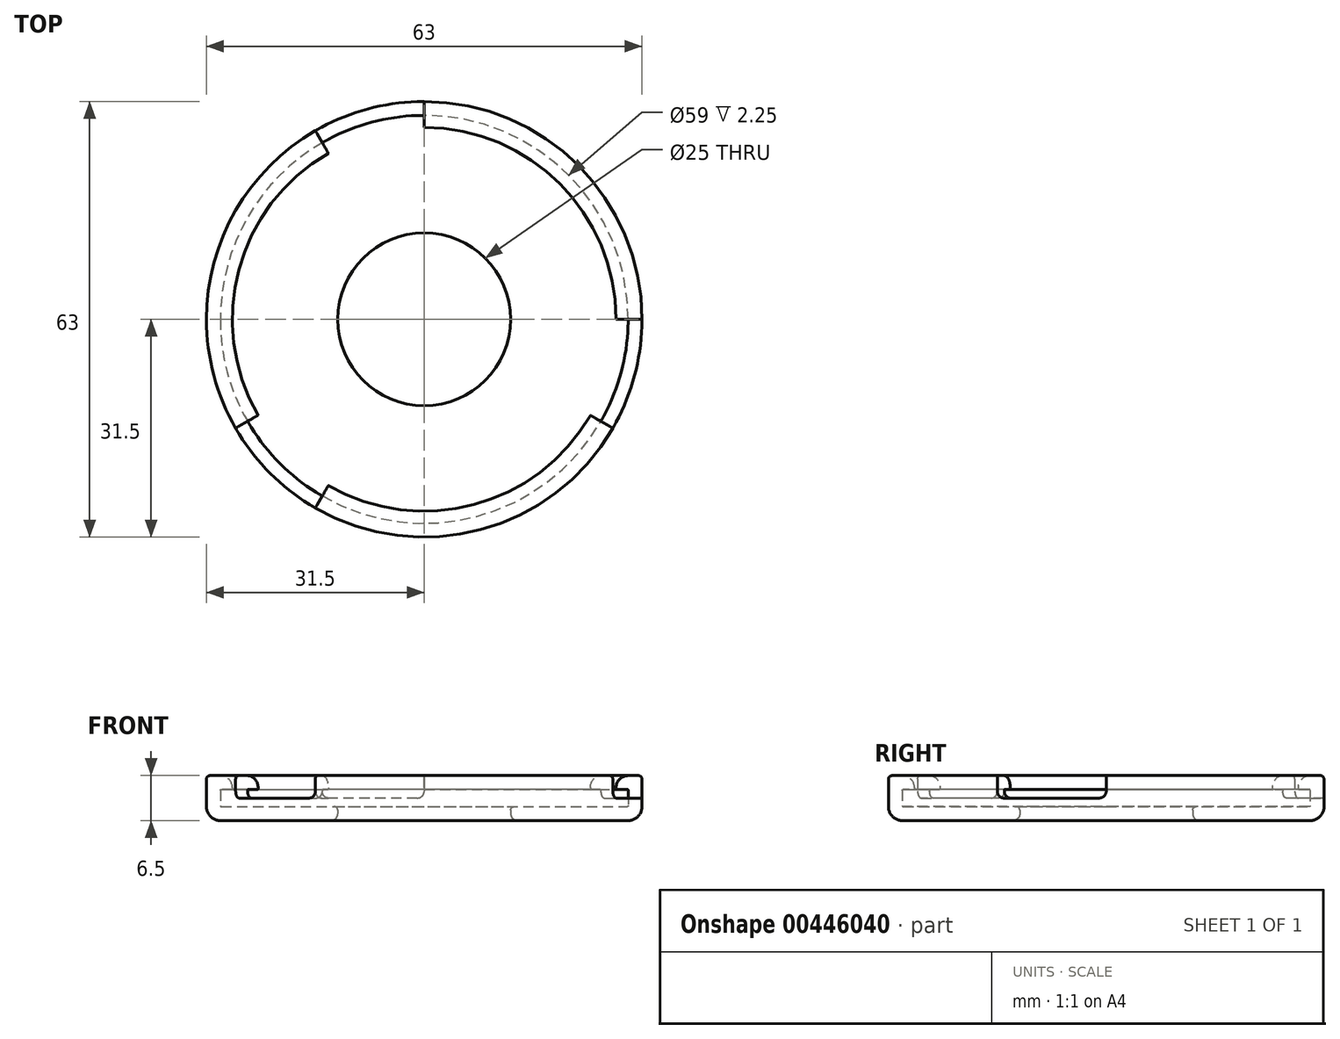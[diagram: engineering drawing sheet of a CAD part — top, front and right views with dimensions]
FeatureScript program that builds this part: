
annotation { "Feature Type Name" : "Feature", "Feature Type Description" : "" }
export const myFeature = defineFeature(function(context is Context, id is Id, definition is map)
    precondition{}
    {
        {
            var Q0;
            Q0=qCreatedBy(makeId("Front.planeOp"),FACE);
            var sketch = newSketch(context, id + "F0", { "sketchPlane" : qUnion([Q0])});
            skLineSegment(sketch, "E0", {"start": v(13.5, 0) * mm, "end": v(29.5, 0) * mm});
            skLineSegment(sketch, "E1", {"start": v(31.5, 2) * mm, "end": v(31.5, 6) * mm});
            skLineSegment(sketch, "E2", {"start": v(31, 6.5) * mm, "end": v(29.5, 6.5) * mm});
            skLineSegment(sketch, "E3", {"start": v(27.75, 4.75) * mm, "end": v(27.75, 4.63) * mm});
            skLineSegment(sketch, "E4", {"start": v(27.88, 4.5) * mm, "end": v(29.38, 4.5) * mm});
            skLineSegment(sketch, "E5", {"start": v(29.5, 4.38) * mm, "end": v(29.5, 2.13) * mm});
            skLineSegment(sketch, "E6", {"start": v(29.38, 2) * mm, "end": v(13, 2) * mm});
            skLineSegment(sketch, "E7", {"start": v(12.5, 1.5) * mm, "end": v(12.5, 1) * mm});
            skPoint(sketch, "E8.visualSharp", {"position": v(31.5, 0) * mm});
            skArc(sketch, "E8.filletArc", {"start": v(29.5, 0) * mm, "mid": v(30.91, 0.59) * mm, "end": v(31.5, 2) * mm});
            skPoint(sketch, "E9.visualSharp", {"position": v(31.5, 6.5) * mm});
            skArc(sketch, "E9.filletArc", {"start": v(31.5, 6) * mm, "mid": v(31.35, 6.35) * mm, "end": v(31, 6.5) * mm});
            skPoint(sketch, "E10.visualSharp", {"position": v(12.5, 0) * mm});
            skArc(sketch, "E10.filletArc", {"start": v(12.5, 1) * mm, "mid": v(12.8, 0.3) * mm, "end": v(13.5, 0) * mm});
            skPoint(sketch, "E11.visualSharp", {"position": v(12.5, 2) * mm});
            skArc(sketch, "E11.filletArc", {"start": v(13, 2) * mm, "mid": v(12.65, 1.85) * mm, "end": v(12.5, 1.5) * mm});
            skPoint(sketch, "E12.visualSharp", {"position": v(27.75, 6.5) * mm});
            skArc(sketch, "E12.filletArc", {"start": v(29.5, 6.5) * mm, "mid": v(28.26, 5.99) * mm, "end": v(27.75, 4.75) * mm});
            skPoint(sketch, "E13.visualSharp", {"position": v(27.75, 4.5) * mm});
            skArc(sketch, "E13.filletArc", {"start": v(27.75, 4.63) * mm, "mid": v(27.79, 4.54) * mm, "end": v(27.88, 4.5) * mm});
            skArc(sketch, "E14.filletArc", {"start": v(29.38, 2) * mm, "mid": v(29.46, 2.04) * mm, "end": v(29.5, 2.13) * mm});
            skPoint(sketch, "E15.visualSharp", {"position": v(29.5, 4.5) * mm});
            skArc(sketch, "E15.filletArc", {"start": v(29.5, 4.38) * mm, "mid": v(29.46, 4.46) * mm, "end": v(29.38, 4.5) * mm});
            skSolve(sketch);
        }
        {
            var Q0;
            Q0=qCreatedBy(makeId("Front.planeOp"),FACE);
            var sketch = newSketch(context, id + "F1", { "sketchPlane" : qUnion([Q0])});
            skLineSegment(sketch, "E16", {"start": v(0, 0) * mm, "end": v(0, 35.52) * mm, "construction": true});
            skSolve(sketch);
        }
        {
            var Q0;
            Q0=makeQuery(id+"F0.imprint","IMPRINT",FACE,{"disambiguationData":[TD([[makeQuery(id+"F0.imprint","IMPRINT",EDGE,{"derivedFrom":sQuery(id+"F0.wireOp",EDGE,"E0")}),1.0]])]});
            var Q1;
            Q1=sQuery(id+"F1.wireOp",EDGE,"E16");
            revolve(context, id + "F2", {"entities" : qUnion([Q0]), "axis" : qUnion([Q1]), "revolveType" : RevolveType.FULL});
        }
        {
            var Q0;
            Q0=makeQuery(id+"F2.opRevolve","SWEPT_FACE",FACE,{"disambiguationData":[OSD([sQuery(id+"F0.wireOp",EDGE,"E6")])]});
            cPlane(context, id + "F3", {"entities" : qUnion([Q0]), "cplaneType" : CPlaneType.OFFSET, "offset" : 1.25 * mm, "width" : 150 * mm, "height" : 150 * mm});
        }
        {
            var Q0;
            Q0=qCreatedBy(id+"F3.planeOp",FACE);
            var sketch = newSketch(context, id + "F4", { "sketchPlane" : qUnion([Q0])});
            skCircle(sketch, "E17.0", {"center": v(0, 0) * mm, "radius": 29.5 * mm, "construction": true});
            skLineSegment(sketch, "E18", {"start": v(0, 0) * mm, "end": v(0, 50) * mm});
            skLineSegment(sketch, "E19", {"start": v(50, 0) * mm, "end": v(0, 0) * mm});
            skLineSegment(sketch, "E20", {"start": v(0, 0) * mm, "end": v(43.3, -25) * mm});
            skLineSegment(sketch, "E21", {"start": v(-25, -43.3) * mm, "end": v(0, 0) * mm});
            skLineSegment(sketch, "E22", {"start": v(0, 0) * mm, "end": v(-43.3, -25) * mm});
            skLineSegment(sketch, "E23", {"start": v(-25, 43.3) * mm, "end": v(0, 0) * mm});
            skLineSegment(sketch, "E24", {"start": v(-25, 43.3) * mm, "end": v(0, 50) * mm});
            skLineSegment(sketch, "E25", {"start": v(50, 0) * mm, "end": v(43.3, -25) * mm});
            skLineSegment(sketch, "E26", {"start": v(-25, -43.3) * mm, "end": v(-43.3, -25) * mm});
            skSolve(sketch);
        }
        {
            var Q0;
            Q0 = qSketchRegion(id + "F4", true);
            extrude(context, id + "F5", {"entities" : qUnion([Q0]), "operationType" : NewBodyOperationType.REMOVE, "depth" : 25 * mm, "offsetDistance" : 25 * mm});
        }
        {
            var Q0;
            Q0=makeQuery(id+"F5.boolean.opBoolean","COPY",EDGE,{"derivedFrom":makeQuery(id+"F5.opExtrude","CAP_EDGE",EDGE,{"disambiguationData":[OSD([sQuery(id+"F4.wireOp",EDGE,"E18")])],"isStart":true})});
            var Q1;
            Q1=makeQuery(id+"F5.boolean.opBoolean","COPY",EDGE,{"derivedFrom":makeQuery(id+"F5.opExtrude","CAP_EDGE",EDGE,{"disambiguationData":[OSD([sQuery(id+"F4.wireOp",EDGE,"E23")])],"isStart":true})});
            var Q2;
            Q2=makeQuery(id+"F5.boolean.opBoolean","COPY",EDGE,{"derivedFrom":makeQuery(id+"F5.opExtrude","CAP_EDGE",EDGE,{"disambiguationData":[OSD([sQuery(id+"F4.wireOp",EDGE,"E19")])],"isStart":true})});
            var Q3;
            Q3=makeQuery(id+"F5.boolean.opBoolean","COPY",EDGE,{"derivedFrom":makeQuery(id+"F5.opExtrude","CAP_EDGE",EDGE,{"disambiguationData":[OSD([sQuery(id+"F4.wireOp",EDGE,"E20")])],"isStart":true})});
            var Q4;
            Q4=makeQuery(id+"F5.boolean.opBoolean","COPY",EDGE,{"derivedFrom":makeQuery(id+"F5.opExtrude","CAP_EDGE",EDGE,{"disambiguationData":[OSD([sQuery(id+"F4.wireOp",EDGE,"E21")])],"isStart":true})});
            var Q5;
            Q5=makeQuery(id+"F5.boolean.opBoolean","COPY",EDGE,{"derivedFrom":makeQuery(id+"F5.opExtrude","CAP_EDGE",EDGE,{"disambiguationData":[OSD([sQuery(id+"F4.wireOp",EDGE,"E22")])],"isStart":true})});
            fillet(context, id + "F6", {"entities" : qUnion([Q0, Q1, Q2, Q3, Q4, Q5]), "radius" : 1 * mm, "tangentPropagation" : true, "allowEdgeOverflow" : false});
        }
    });
